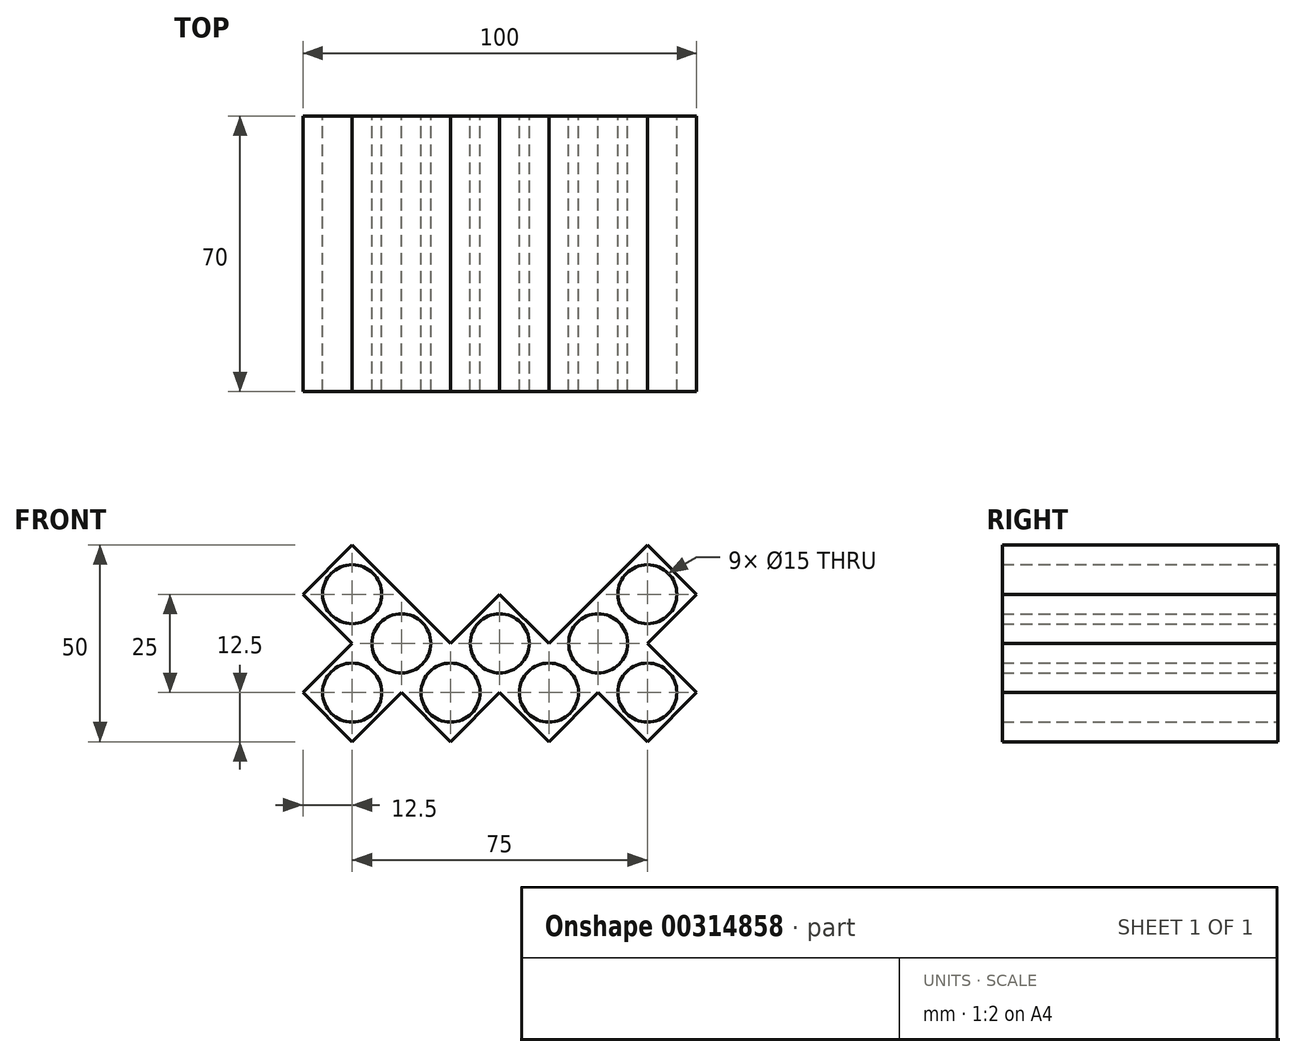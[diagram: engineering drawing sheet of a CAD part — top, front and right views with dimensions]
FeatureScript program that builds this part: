
annotation { "Feature Type Name" : "Feature", "Feature Type Description" : "" }
export const myFeature = defineFeature(function(context is Context, id is Id, definition is map)
    precondition{}
    {
        {
            var Q0;
            Q0=qCreatedBy(makeId("Front.planeOp"),FACE);
            var sketch = newSketch(context, id + "F0", { "sketchPlane" : qUnion([Q0])});
            skLineSegment(sketch, "E0", {"start": v(-25, 0) * mm, "end": v(-12.5, -12.5) * mm});
            skLineSegment(sketch, "E1", {"start": v(-12.5, -12.5) * mm, "end": v(0, 0) * mm});
            skLineSegment(sketch, "E2", {"start": v(0, 0) * mm, "end": v(-12.5, 12.5) * mm});
            skLineSegment(sketch, "E3", {"start": v(-12.5, 12.5) * mm, "end": v(-25, 0) * mm});
            skPoint(sketch, "E4", {"position": v(-12.5, 0) * mm});
            skLineSegment(sketch, "E5", {"start": v(12.5, 12.5) * mm, "end": v(0, 0) * mm});
            skLineSegment(sketch, "E6", {"start": v(0, 0) * mm, "end": v(12.5, -12.5) * mm});
            skLineSegment(sketch, "E7", {"start": v(12.5, -12.5) * mm, "end": v(25, 0) * mm});
            skLineSegment(sketch, "E8", {"start": v(25, 0) * mm, "end": v(12.5, 12.5) * mm});
            skPoint(sketch, "E9", {"position": v(12.5, 0) * mm});
            skLineSegment(sketch, "E10", {"start": v(-12.5, -12.5) * mm, "end": v(0, -25) * mm});
            skLineSegment(sketch, "E11", {"start": v(0, -25) * mm, "end": v(12.5, -12.5) * mm});
            skPoint(sketch, "E12", {"position": v(0, -12.5) * mm});
            skLineSegment(sketch, "E13", {"start": v(25, 0) * mm, "end": v(37.5, -12.5) * mm});
            skLineSegment(sketch, "E14", {"start": v(12.5, -12.5) * mm, "end": v(25, -25) * mm});
            skLineSegment(sketch, "E15", {"start": v(25, -25) * mm, "end": v(37.5, -12.5) * mm});
            skPoint(sketch, "E16", {"position": v(25, -12.5) * mm});
            skPoint(sketch, "E17.endSnap0", {"position": v(-25, -12.5) * mm});
            skLineSegment(sketch, "E18", {"start": v(-25, 0) * mm, "end": v(-37.5, -12.5) * mm});
            skLineSegment(sketch, "E19", {"start": v(-37.5, -12.5) * mm, "end": v(-25, -25) * mm});
            skLineSegment(sketch, "E20", {"start": v(-25, -25) * mm, "end": v(-12.5, -12.5) * mm});
            skPoint(sketch, "E21", {"position": v(37.5, 0) * mm});
            skLineSegment(sketch, "E22", {"start": v(37.5, -12.5) * mm, "end": v(50, 0) * mm});
            skLineSegment(sketch, "E23", {"start": v(50, 0) * mm, "end": v(37.5, 12.5) * mm});
            skLineSegment(sketch, "E24", {"start": v(37.5, 12.5) * mm, "end": v(25, 0) * mm});
            skLineSegment(sketch, "E25", {"start": v(50, 0) * mm, "end": v(62.5, -12.5) * mm});
            skPoint(sketch, "E26", {"position": v(50, -12.5) * mm});
            skLineSegment(sketch, "E27", {"start": v(37.5, -12.5) * mm, "end": v(50, -25) * mm});
            skLineSegment(sketch, "E28", {"start": v(50, -25) * mm, "end": v(62.5, -12.5) * mm});
            skLineSegment(sketch, "E29", {"start": v(-37.5, 12.5) * mm, "end": v(-25, 0) * mm});
            skLineSegment(sketch, "E30", {"start": v(-25, 25) * mm, "end": v(-12.5, 12.5) * mm});
            skLineSegment(sketch, "E31", {"start": v(-25, 25) * mm, "end": v(-37.5, 12.5) * mm});
            skPoint(sketch, "E32", {"position": v(-25, 12.5) * mm});
            skLineSegment(sketch, "E33", {"start": v(50, 0) * mm, "end": v(62.5, 12.5) * mm});
            skLineSegment(sketch, "E34", {"start": v(37.5, 12.5) * mm, "end": v(50, 25) * mm});
            skLineSegment(sketch, "E35", {"start": v(50, 25) * mm, "end": v(62.5, 12.5) * mm});
            skPoint(sketch, "E36", {"position": v(50, 12.5) * mm});
            skSolve(sketch);
        }
        {
            var Q0;
            Q0=makeQuery(id+"F0.imprint","IMPRINT",FACE,{"disambiguationData":[TD([[makeQuery(id+"F0.imprint","IMPRINT",EDGE,{"derivedFrom":sQuery(id+"F0.wireOp",EDGE,"E1")}),-1.0]])]});
            var Q1;
            Q1=makeQuery(id+"F0.imprint","IMPRINT",FACE,{"disambiguationData":[TD([[makeQuery(id+"F0.imprint","IMPRINT",EDGE,{"derivedFrom":sQuery(id+"F0.wireOp",EDGE,"E5")}),1.0]])]});
            var Q2;
            Q2=makeQuery(id+"F0.imprint","IMPRINT",FACE,{"disambiguationData":[TD([[makeQuery(id+"F0.imprint","IMPRINT",EDGE,{"derivedFrom":sQuery(id+"F0.wireOp",EDGE,"E7")}),-1.0]])]});
            var Q3;
            Q3=makeQuery(id+"F0.imprint","IMPRINT",FACE,{"disambiguationData":[TD([[makeQuery(id+"F0.imprint","IMPRINT",EDGE,{"derivedFrom":sQuery(id+"F0.wireOp",EDGE,"E13")}),1.0]])]});
            var Q4;
            Q4=makeQuery(id+"F0.imprint","IMPRINT",FACE,{"disambiguationData":[TD([[makeQuery(id+"F0.imprint","IMPRINT",EDGE,{"derivedFrom":sQuery(id+"F0.wireOp",EDGE,"E22")}),-1.0]])]});
            var Q5;
            Q5=makeQuery(id+"F0.imprint","IMPRINT",FACE,{"disambiguationData":[TD([[makeQuery(id+"F0.imprint","IMPRINT",EDGE,{"derivedFrom":sQuery(id+"F0.wireOp",EDGE,"E23")}),-1.0]])]});
            var Q6;
            Q6=makeQuery(id+"F0.imprint","IMPRINT",FACE,{"disambiguationData":[TD([[makeQuery(id+"F0.imprint","IMPRINT",EDGE,{"derivedFrom":sQuery(id+"F0.wireOp",EDGE,"E0")}),1.0]])]});
            var Q7;
            Q7=makeQuery(id+"F0.imprint","IMPRINT",FACE,{"disambiguationData":[TD([[makeQuery(id+"F0.imprint","IMPRINT",EDGE,{"derivedFrom":sQuery(id+"F0.wireOp",EDGE,"E0")}),-1.0]])]});
            var Q8;
            Q8=makeQuery(id+"F0.imprint","IMPRINT",FACE,{"disambiguationData":[TD([[makeQuery(id+"F0.imprint","IMPRINT",EDGE,{"derivedFrom":sQuery(id+"F0.wireOp",EDGE,"E3")}),-1.0]])]});
            extrude(context, id + "F1", {"entities" : qUnion([Q0, Q1, Q2, Q3, Q4, Q5, Q6, Q7, Q8]), "depth" : 70 * mm});
        }
        {
            var Q0;
            Q0=sQuery(id+"F0.wireOp",VERTEX,"E4");
            var Q1;
            Q1=sQuery(id+"F0.wireOp",VERTEX,"E17.endSnap0");
            var Q2;
            Q2=sQuery(id+"F0.wireOp",VERTEX,"E12");
            var Q3;
            Q3=sQuery(id+"F0.wireOp",VERTEX,"E9");
            var Q4;
            Q4=sQuery(id+"F0.wireOp",VERTEX,"E16");
            var Q5;
            Q5=sQuery(id+"F0.wireOp",VERTEX,"E26");
            var Q6;
            Q6=sQuery(id+"F0.wireOp",VERTEX,"E21");
            var Q7;
            Q7=sQuery(id+"F0.wireOp",VERTEX,"E32");
            var Q8;
            Q8=sQuery(id+"F0.wireOp",VERTEX,"E36");
            var Q9;
            Q9=makeQuery(id+"F1.opExtrude","SWEPT_BODY",BODY,{"disambiguationData":[OSD([sQuery(id+"F0.wireOp",EDGE,"E0"),sQuery(id+"F0.wireOp",EDGE,"E1"),sQuery(id+"F0.wireOp",EDGE,"E2"),sQuery(id+"F0.wireOp",EDGE,"E3")])]});
            hole(context, id + "F2", {"style" : HoleStyle.SIMPLE, "endStyle" : HoleEndStyle.THROUGH, "oppositeDirection" : true, "holeDiameter" : 15 * mm, "tappedDepth" : 12 * mm, "tapClearance" : 3, "locations" : qUnion([Q0, Q1, Q2, Q3, Q4, Q5, Q6, Q7, Q8]), "scope" : qUnion([Q9])});
        }
    });
